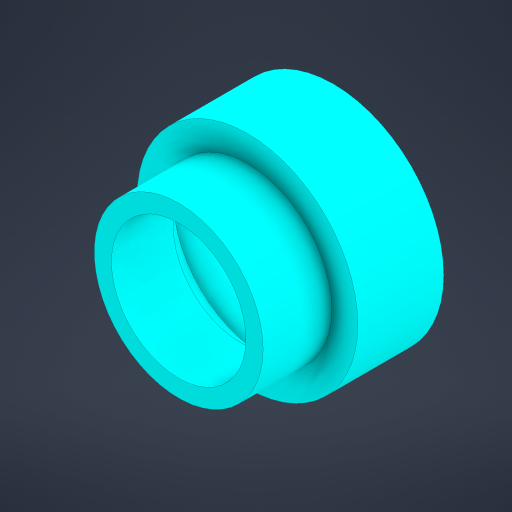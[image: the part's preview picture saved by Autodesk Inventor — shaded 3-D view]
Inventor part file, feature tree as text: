
AUTODESK INVENTOR PART (.ipt)
format: ipt  version: 2023.4 (Build 274418000, 418)  size: 216,576 bytes
history: native  units: mm
features: extrude x3, sketch x1, chamfer x1
ambient origin geometry x8: Origin, YZ Plane, XZ Plane, XY Plane, X Axis, Y Axis, Z Axis, Center Point
bodies: Solid1 (feature_tree)
feature tree (5):
  sketch  "Sketch1"  dims[d0=12.2875mm d1=1.25mm d2=5.0mm d3=0.0mm d4=26.25mm d5=13.5675mm d6=1.25mm d7=1.25mm d8=1.25mm d9=0.0mm d10=5.0mm d11=0.0mm d12=1.75mm d13=2.0mm d14=45.0deg]
  extrude  "Extrusion1"  Depth=1.25mm
  extrude  "Extrusion2"  Depth=5.0mm TaperAngle=0.0deg
  extrude  "Extrusion3"  Depth=5.0mm
  chamfer  "Chamfer1"  Distance=13.5675mm
